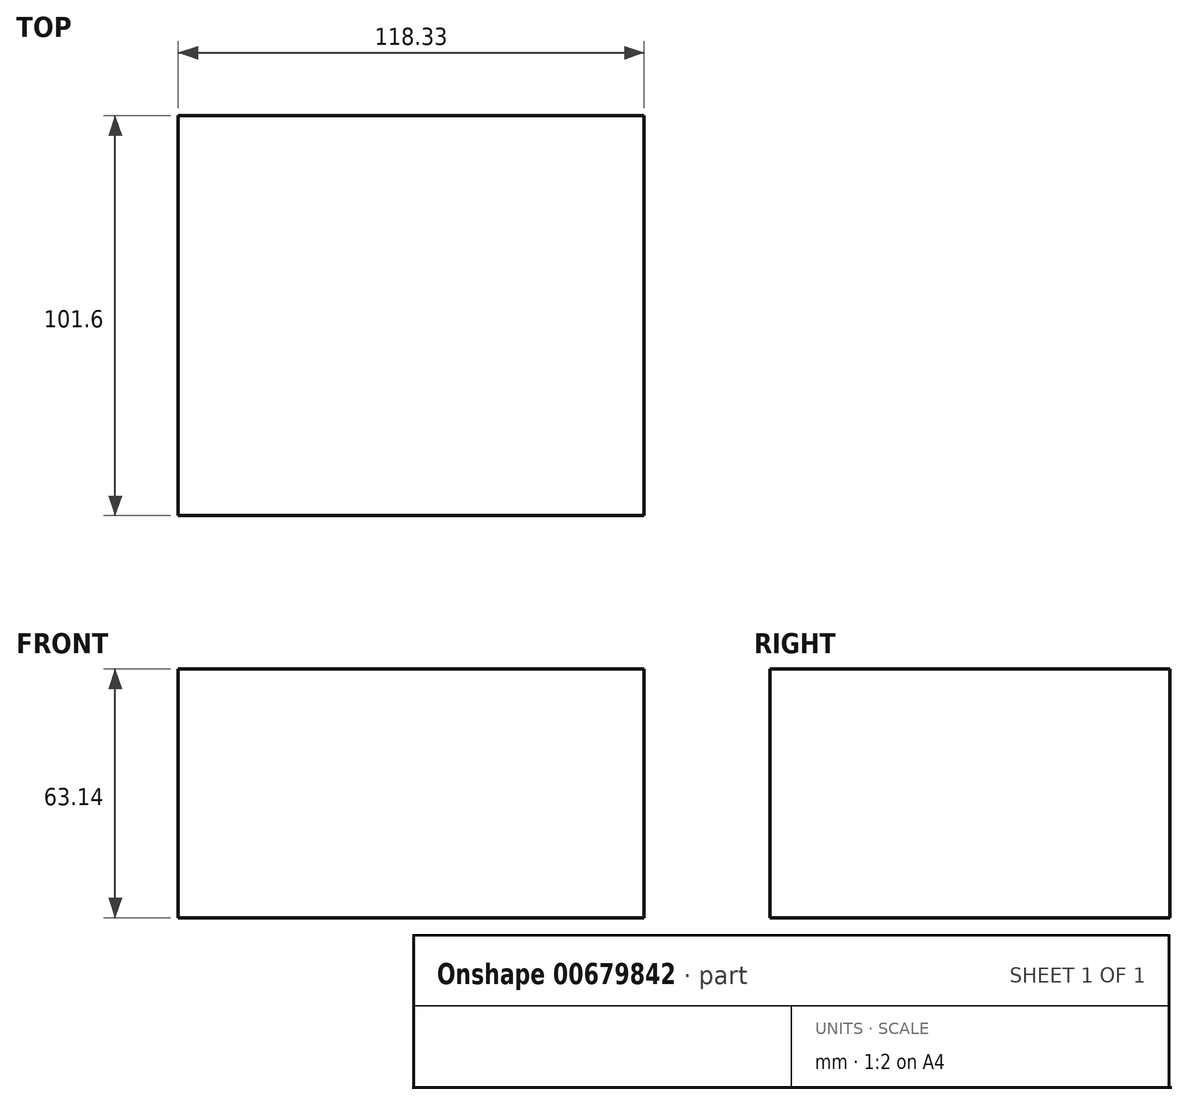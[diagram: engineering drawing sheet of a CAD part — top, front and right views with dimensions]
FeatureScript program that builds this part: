
annotation { "Feature Type Name" : "Feature", "Feature Type Description" : "" }
export const myFeature = defineFeature(function(context is Context, id is Id, definition is map)
    precondition{}
    {
        {
            var Q0;
            Q0=qCreatedBy(makeId("Front.planeOp"),FACE);
            var sketch = newSketch(context, id + "F0", { "sketchPlane" : qUnion([Q0])});
            skLineSegment(sketch, "E0.bottom", {"start": v(-57.24, 34.58) * mm, "end": v(61.1, 34.58) * mm});
            skLineSegment(sketch, "E0.top", {"start": v(-57.24, -28.56) * mm, "end": v(61.1, -28.56) * mm});
            skLineSegment(sketch, "E0.left", {"start": v(-57.24, 34.58) * mm, "end": v(-57.24, -28.56) * mm});
            skLineSegment(sketch, "E0.right", {"start": v(61.1, 34.58) * mm, "end": v(61.1, -28.56) * mm});
            skSolve(sketch);
        }
        {
            var Q0;
            Q0 = qSketchRegion(id + "F0", true);
            extrude(context, id + "F1", {"entities" : qUnion([Q0]), "depth" : 101.6 * mm, "offsetDistance" : 25.4 * mm});
        }
    });
